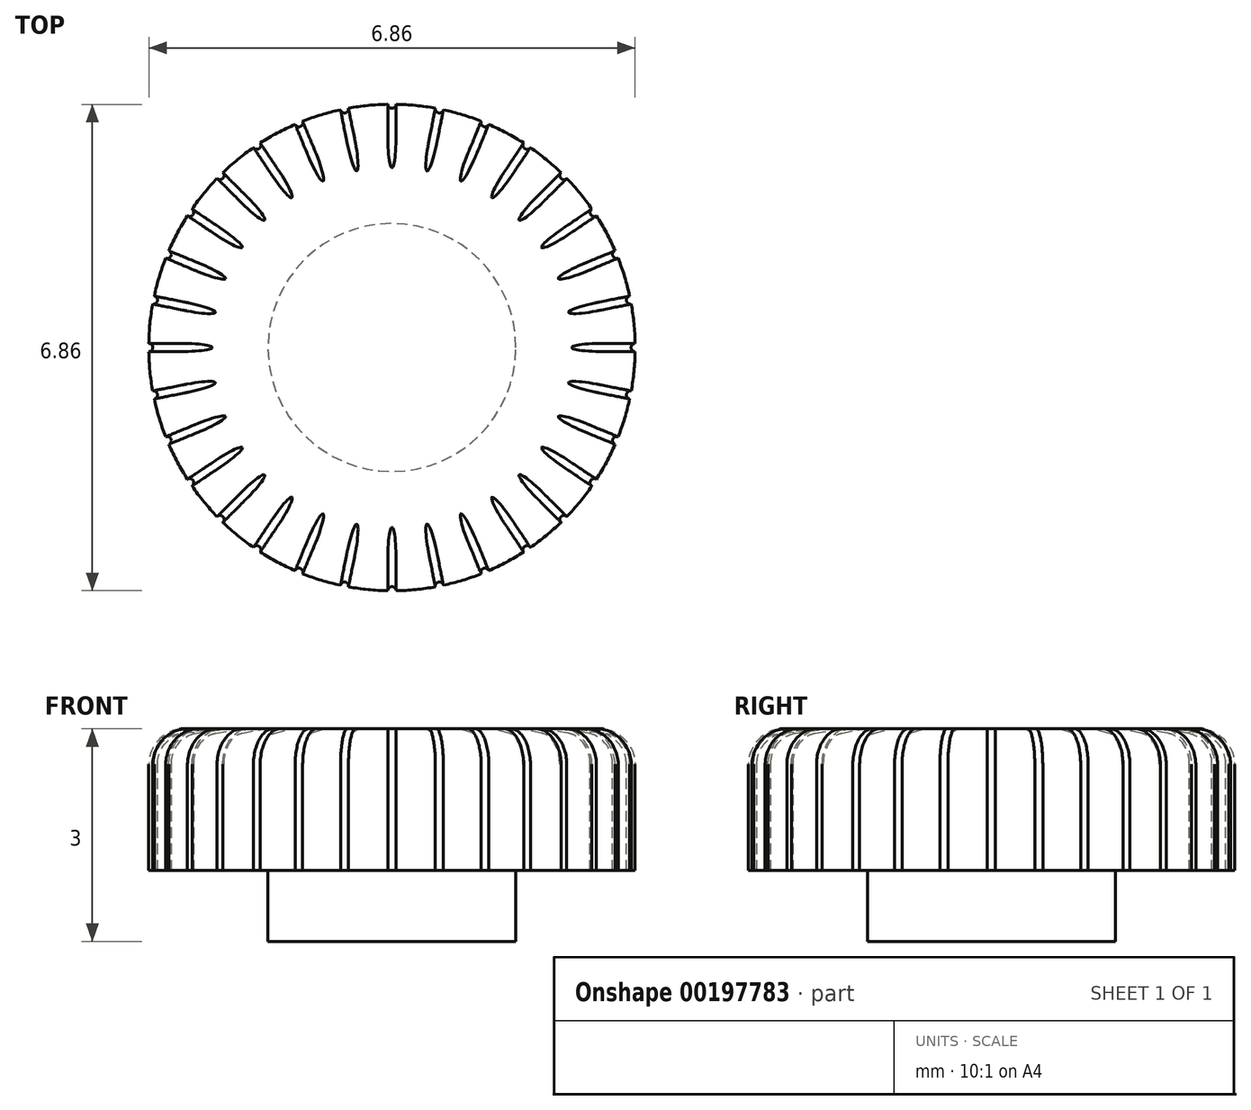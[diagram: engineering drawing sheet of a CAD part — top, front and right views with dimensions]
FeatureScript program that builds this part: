
annotation { "Feature Type Name" : "Feature", "Feature Type Description" : "" }
export const myFeature = defineFeature(function(context is Context, id is Id, definition is map)
    precondition{}
    {
        {
            var Q0;
            Q0=qCreatedBy(makeId("Top.planeOp"),FACE);
            var sketch = newSketch(context, id + "F0", { "sketchPlane" : qUnion([Q0])});
            skCircle(sketch, "E0", {"center": v(0, 0) * mm, "radius": 1.75 * mm});
            skSolve(sketch);
        }
        {
            var Q0;
            Q0 = qSketchRegion(id + "F0", true);
            extrude(context, id + "F1", {"entities" : qUnion([Q0]), "depth" : 1 * mm});
        }
        {
            var Q0;
            Q0=makeQuery(id+"F1.opExtrude","CAP_FACE",FACE,{"disambiguationData":[OSD([sQuery(id+"F0.wireOp",EDGE,"E0")])],"isStart":false});
            var sketch = newSketch(context, id + "F2", { "sketchPlane" : qUnion([Q0])});
            skCircle(sketch, "E1", {"center": v(0, 0) * mm, "radius": 3.43 * mm});
            skSolve(sketch);
        }
        {
            var Q0;
            Q0 = qSketchRegion(id + "F2", true);
            extrude(context, id + "F3", {"entities" : qUnion([Q0]), "operationType" : NewBodyOperationType.ADD, "depth" : 2 * mm});
        }
        {
            var Q0;
            Q0=makeQuery(id+"F3.opExtrude","CAP_FACE",FACE,{"disambiguationData":[OSD([sQuery(id+"F2.wireOp",EDGE,"E1")])],"isStart":false});
            fillet(context, id + "F4", {"entities" : qUnion([Q0]), "radius" : 0.5 * mm, "tangentPropagation" : true, "allowEdgeOverflow" : false});
        }
        {
            var Q0;
            Q0=makeQuery(id+"F3.opExtrude","CAP_FACE",FACE,{"disambiguationData":[OSD([sQuery(id+"F2.wireOp",EDGE,"E1")])],"isStart":true});
            var sketch = newSketch(context, id + "F5", { "sketchPlane" : qUnion([Q0])});
            skCircle(sketch, "E2", {"center": v(0, -3.43) * mm, "radius": 0.06 * mm});
            skSolve(sketch);
        }
        {
            var Q0;
            Q0=qCreatedBy(makeId("Right.planeOp"),FACE);
            var sketch = newSketch(context, id + "F6", { "sketchPlane" : qUnion([Q0])});
            skLineSegment(sketch, "E3", {"start": v(3.43, 2.5) * mm, "end": v(3.43, 1) * mm});
            skArc(sketch, "E4", {"start": v(3.43, 2.5) * mm, "mid": v(3.3, 2.83) * mm, "end": v(3, 3) * mm});
            skLineSegment(sketch, "E5", {"start": v(3, 3) * mm, "end": v(2.5, 3.06) * mm});
            skLineSegment(sketch, "E6", {"start": v(2.93, 2.5) * mm, "end": v(3, 3) * mm, "construction": true});
            skSolve(sketch);
        }
        {
            var Q0;
            {var subQ0=sQuery(id+"F5.wireOp",EDGE,"E2");var subQ1=makeQuery(id+"F3.opExtrude","CAP_EDGE",EDGE,{"disambiguationData":[OSD([sQuery(id+"F2.wireOp",EDGE,"E1")])],"isStart":true});var subQ2=makeQuery(id+"F5.imprint","INTERSECT",VERTEX,{"disambiguationData":[OD(0.0)],"derivedFrom":[subQ1,subQ0]});Q0=makeQuery(id+"F5.imprint","IMPRINT",FACE,{"disambiguationData":[TD([[makeQuery(id+"F5.imprint","IMPRINT",EDGE,{"disambiguationData":[TD([[subQ2,-1.0]])],"derivedFrom":subQ0}),1.0]])]});}
            var Q1;
            {var subQ0=sQuery(id+"F5.wireOp",EDGE,"E2");var subQ1=makeQuery(id+"F3.opExtrude","CAP_EDGE",EDGE,{"disambiguationData":[OSD([sQuery(id+"F2.wireOp",EDGE,"E1")])],"isStart":true});var subQ2=makeQuery(id+"F5.imprint","INTERSECT",VERTEX,{"disambiguationData":[OD(0.0)],"derivedFrom":[subQ1,subQ0]});Q1=makeQuery(id+"F5.imprint","IMPRINT",FACE,{"disambiguationData":[TD([[makeQuery(id+"F5.imprint","IMPRINT",EDGE,{"disambiguationData":[TD([[subQ2,1.0]])],"derivedFrom":subQ0}),1.0]])]});}
            var Q2;
            Q2=sQuery(id+"F6.wireOp",EDGE,"E3");
            var Q3;
            Q3=sQuery(id+"F6.wireOp",EDGE,"E4");
            var Q4;
            Q4=sQuery(id+"F6.wireOp",EDGE,"E5");
            sweep(context, id + "F7", {"profiles" : qUnion([Q0, Q1]), "path" : qUnion([Q2, Q3, Q4])});
        }
        {
            var Q0;
            Q0=makeQuery(id+"F7.opSweep","SWEPT_BODY",BODY,{"disambiguationData":[OSD([sQuery(id+"F5.wireOp",EDGE,"E2"),sQuery(id+"F6.wireOp",EDGE,"E5")])]});
            var Q1;
            {var subQ0=sQuery(id+"F2.wireOp",EDGE,"E1");Q1=makeQuery(id+"F4.opFillet","BLEND_EDGE",EDGE,{"blendedFrom":[makeQuery(id+"F3.opExtrude","CAP_EDGE",EDGE,{"disambiguationData":[OSD([subQ0])],"isStart":false}),makeQuery(id+"F3.opExtrude","CAP_FACE",FACE,{"disambiguationData":[OSD([subQ0])],"isStart":false})],"blendedInto":[makeQuery(id+"F3.opExtrude","CAP_FACE",FACE,{"disambiguationData":[OSD([subQ0])],"isStart":false})]});}
            circularPattern(context, id + "F8", {"operationType" : NewBodyOperationType.REMOVE, "entities" : qUnion([Q0]), "axis" : qUnion([Q1]), "angle" : 360 * degree, "instanceCount" : 32, "equalSpace" : true});
        }
    });
